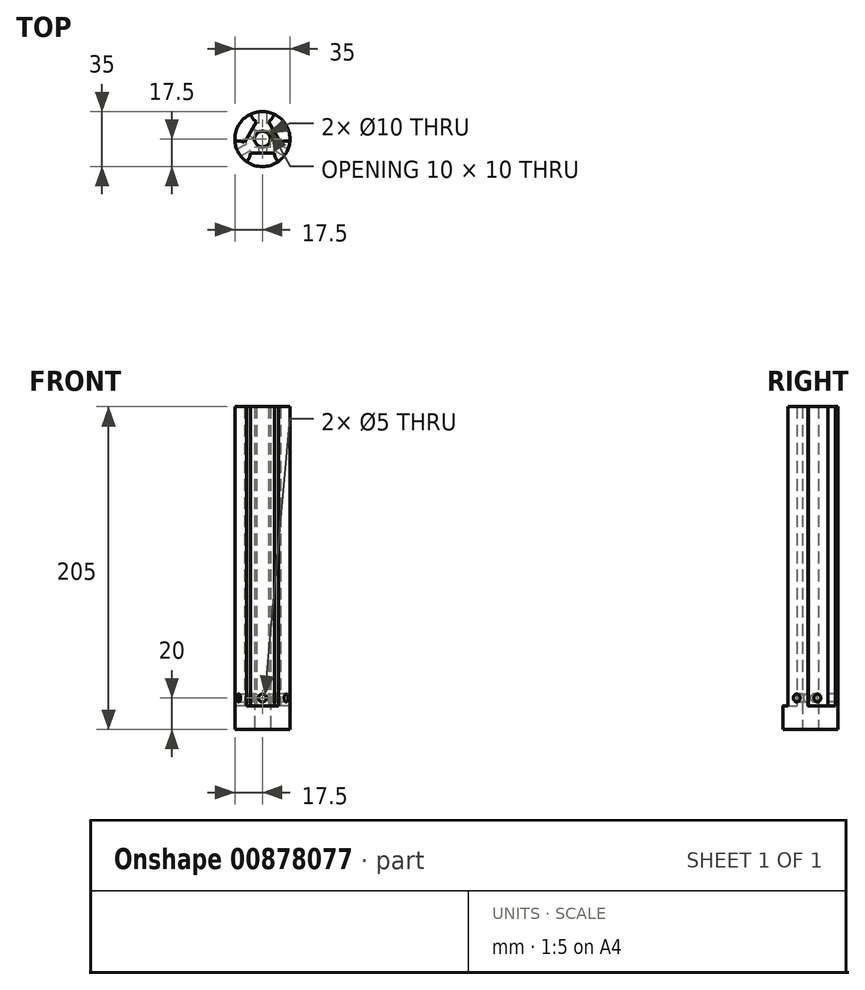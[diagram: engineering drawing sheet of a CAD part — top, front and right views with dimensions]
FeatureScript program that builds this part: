
annotation { "Feature Type Name" : "Feature", "Feature Type Description" : "" }
export const myFeature = defineFeature(function(context is Context, id is Id, definition is map)
    precondition{}
    {
        {
            var Q0;
            Q0=qCreatedBy(makeId("Top.planeOp"),FACE);
            var sketch = newSketch(context, id + "F0", { "sketchPlane" : qUnion([Q0])});
            skCircle(sketch, "E0", {"center": v(0, 0) * mm, "radius": 17.5 * mm});
            skCircle(sketch, "E1.cCircle", {"center": v(0, 0) * mm, "radius": 17.5 * mm, "construction": true});
            skLineSegment(sketch, "E1.0", {"start": v(0, 17.5) * mm, "end": v(15.16, -8.75) * mm});
            skLineSegment(sketch, "E1.1", {"start": v(15.16, -8.75) * mm, "end": v(-15.16, -8.75) * mm});
            skLineSegment(sketch, "E1.2", {"start": v(-15.16, -8.75) * mm, "end": v(0, 17.5) * mm});
            skCircle(sketch, "E2", {"center": v(-15.16, -8.75) * mm, "radius": 7.5 * mm});
            skCircle(sketch, "E3", {"center": v(0, 17.5) * mm, "radius": 7.5 * mm});
            skCircle(sketch, "E4", {"center": v(15.16, -8.75) * mm, "radius": 7.5 * mm});
            skPoint(sketch, "E5", {"position": v(-3.75, 11) * mm});
            skPoint(sketch, "E6", {"position": v(-11.4, -2.25) * mm});
            skCircle(sketch, "E7", {"center": v(0, 0) * mm, "radius": 5 * mm});
            skSolve(sketch);
        }
        {
            var Q0;
            {var subQ0=sQuery(id+"F0.wireOp",EDGE,"E3");var subQ1=sQuery(id+"F0.wireOp",EDGE,"E0");var subQ2=makeQuery(id+"F0.imprint","INTERSECT",VERTEX,{"disambiguationData":[OD(1.0)],"derivedFrom":[subQ1,subQ0]});Q0=makeQuery(id+"F0.imprint","IMPRINT",FACE,{"disambiguationData":[TD([[makeQuery(id+"F0.imprint","IMPRINT",EDGE,{"disambiguationData":[TD([[subQ2,-1.0]])],"derivedFrom":subQ1}),1.0]])]});}
            var Q1;
            {var subQ1=sQuery(id+"F0.wireOp",EDGE,"E0");var subQ3=sQuery(id+"F0.wireOp",EDGE,"E3");var subQ4=makeQuery(id+"F0.imprint","INTERSECT",VERTEX,{"disambiguationData":[OD(1.0)],"derivedFrom":[subQ1,subQ3]});Q1=makeQuery(id+"F0.imprint","IMPRINT",FACE,{"disambiguationData":[TD([[makeQuery(id+"F0.imprint","IMPRINT",EDGE,{"disambiguationData":[TD([[subQ4,-1.0]])],"derivedFrom":subQ3}),1.0]])]});}
            var Q2;
            {var subQ1=sQuery(id+"F0.wireOp",EDGE,"E1.0");var subQ3=sQuery(id+"F0.wireOp",EDGE,"E3");var subQ4=makeQuery(id+"F0.imprint","INTERSECT",VERTEX,{"derivedFrom":[subQ1,subQ3]});Q2=makeQuery(id+"F0.imprint","IMPRINT",FACE,{"disambiguationData":[TD([[makeQuery(id+"F0.imprint","IMPRINT",EDGE,{"disambiguationData":[TD([[subQ4,1.0]])],"derivedFrom":subQ3}),1.0]])]});}
            var Q3;
            {var subQ1=sQuery(id+"F0.wireOp",EDGE,"E0");var subQ3=sQuery(id+"F0.wireOp",EDGE,"E3");var subQ4=makeQuery(id+"F0.imprint","INTERSECT",VERTEX,{"disambiguationData":[OD(0.0)],"derivedFrom":[subQ1,subQ3]});Q3=makeQuery(id+"F0.imprint","IMPRINT",FACE,{"disambiguationData":[TD([[makeQuery(id+"F0.imprint","IMPRINT",EDGE,{"disambiguationData":[TD([[subQ4,1.0]])],"derivedFrom":subQ3}),1.0]])]});}
            var Q4;
            {var subQ0=sQuery(id+"F0.wireOp",EDGE,"E3");var subQ1=sQuery(id+"F0.wireOp",EDGE,"E0");var subQ2=makeQuery(id+"F0.imprint","INTERSECT",VERTEX,{"disambiguationData":[OD(0.0)],"derivedFrom":[subQ1,subQ0]});Q4=makeQuery(id+"F0.imprint","IMPRINT",FACE,{"disambiguationData":[TD([[makeQuery(id+"F0.imprint","IMPRINT",EDGE,{"disambiguationData":[TD([[subQ2,1.0]])],"derivedFrom":subQ1}),1.0]])]});}
            var Q5;
            Q5=makeQuery(id+"F0.imprint","IMPRINT",FACE,{"disambiguationData":[TD([[makeQuery(id+"F0.imprint","IMPRINT",EDGE,{"derivedFrom":sQuery(id+"F0.wireOp",EDGE,"E7")}),-1.0]])]});
            var Q6;
            {var subQ1=sQuery(id+"F0.wireOp",EDGE,"E1.1");var subQ3=sQuery(id+"F0.wireOp",EDGE,"E2");var subQ4=makeQuery(id+"F0.imprint","INTERSECT",VERTEX,{"derivedFrom":[subQ1,subQ3]});Q6=makeQuery(id+"F0.imprint","IMPRINT",FACE,{"disambiguationData":[TD([[makeQuery(id+"F0.imprint","IMPRINT",EDGE,{"disambiguationData":[TD([[subQ4,-1.0]])],"derivedFrom":subQ3}),1.0]])]});}
            var Q7;
            {var subQ1=sQuery(id+"F0.wireOp",EDGE,"E0");var subQ3=sQuery(id+"F0.wireOp",EDGE,"E2");var subQ4=makeQuery(id+"F0.imprint","INTERSECT",VERTEX,{"disambiguationData":[OD(0.0)],"derivedFrom":[subQ1,subQ3]});Q7=makeQuery(id+"F0.imprint","IMPRINT",FACE,{"disambiguationData":[TD([[makeQuery(id+"F0.imprint","IMPRINT",EDGE,{"disambiguationData":[TD([[subQ4,1.0]])],"derivedFrom":subQ3}),1.0]])]});}
            var Q8;
            {var subQ0=sQuery(id+"F0.wireOp",EDGE,"E2");var subQ1=sQuery(id+"F0.wireOp",EDGE,"E0");var subQ2=makeQuery(id+"F0.imprint","INTERSECT",VERTEX,{"disambiguationData":[OD(1.0)],"derivedFrom":[subQ1,subQ0]});Q8=makeQuery(id+"F0.imprint","IMPRINT",FACE,{"disambiguationData":[TD([[makeQuery(id+"F0.imprint","IMPRINT",EDGE,{"disambiguationData":[TD([[subQ2,-1.0]])],"derivedFrom":subQ1}),1.0]])]});}
            var Q9;
            {var subQ1=sQuery(id+"F0.wireOp",EDGE,"E0");var subQ3=sQuery(id+"F0.wireOp",EDGE,"E2");var subQ4=makeQuery(id+"F0.imprint","INTERSECT",VERTEX,{"disambiguationData":[OD(1.0)],"derivedFrom":[subQ1,subQ3]});Q9=makeQuery(id+"F0.imprint","IMPRINT",FACE,{"disambiguationData":[TD([[makeQuery(id+"F0.imprint","IMPRINT",EDGE,{"disambiguationData":[TD([[subQ4,-1.0]])],"derivedFrom":subQ3}),1.0]])]});}
            var Q10;
            {var subQ1=sQuery(id+"F0.wireOp",EDGE,"E0");var subQ3=sQuery(id+"F0.wireOp",EDGE,"E4");var subQ4=makeQuery(id+"F0.imprint","INTERSECT",VERTEX,{"disambiguationData":[OD(0.0)],"derivedFrom":[subQ1,subQ3]});Q10=makeQuery(id+"F0.imprint","IMPRINT",FACE,{"disambiguationData":[TD([[makeQuery(id+"F0.imprint","IMPRINT",EDGE,{"disambiguationData":[TD([[subQ4,1.0]])],"derivedFrom":subQ3}),1.0]])]});}
            var Q11;
            {var subQ1=sQuery(id+"F0.wireOp",EDGE,"E1.0");var subQ3=sQuery(id+"F0.wireOp",EDGE,"E4");var subQ4=makeQuery(id+"F0.imprint","INTERSECT",VERTEX,{"derivedFrom":[subQ1,subQ3]});Q11=makeQuery(id+"F0.imprint","IMPRINT",FACE,{"disambiguationData":[TD([[makeQuery(id+"F0.imprint","IMPRINT",EDGE,{"disambiguationData":[TD([[subQ4,-1.0]])],"derivedFrom":subQ3}),1.0]])]});}
            var Q12;
            {var subQ1=sQuery(id+"F0.wireOp",EDGE,"E0");var subQ3=sQuery(id+"F0.wireOp",EDGE,"E4");var subQ4=makeQuery(id+"F0.imprint","INTERSECT",VERTEX,{"disambiguationData":[OD(1.0)],"derivedFrom":[subQ1,subQ3]});Q12=makeQuery(id+"F0.imprint","IMPRINT",FACE,{"disambiguationData":[TD([[makeQuery(id+"F0.imprint","IMPRINT",EDGE,{"disambiguationData":[TD([[subQ4,-1.0]])],"derivedFrom":subQ3}),1.0]])]});}
            extrude(context, id + "F1", {"entities" : qUnion([Q0, Q1, Q2, Q3, Q4, Q5, Q6, Q7, Q8, Q9, Q10, Q11, Q12]), "depth" : 15 * mm, "offsetDistance" : 25 * mm});
        }
        {
            var Q0;
            {var subQ1=sQuery(id+"F0.wireOp",EDGE,"E0");var subQ3=sQuery(id+"F0.wireOp",EDGE,"E3");var subQ4=makeQuery(id+"F0.imprint","INTERSECT",VERTEX,{"disambiguationData":[OD(1.0)],"derivedFrom":[subQ1,subQ3]});Q0=makeQuery(id+"F0.imprint","IMPRINT",FACE,{"disambiguationData":[TD([[makeQuery(id+"F0.imprint","IMPRINT",EDGE,{"disambiguationData":[TD([[subQ4,-1.0]])],"derivedFrom":subQ3}),1.0]])]});}
            var Q1;
            {var subQ1=sQuery(id+"F0.wireOp",EDGE,"E1.0");var subQ3=sQuery(id+"F0.wireOp",EDGE,"E3");var subQ4=makeQuery(id+"F0.imprint","INTERSECT",VERTEX,{"derivedFrom":[subQ1,subQ3]});Q1=makeQuery(id+"F0.imprint","IMPRINT",FACE,{"disambiguationData":[TD([[makeQuery(id+"F0.imprint","IMPRINT",EDGE,{"disambiguationData":[TD([[subQ4,1.0]])],"derivedFrom":subQ3}),1.0]])]});}
            var Q2;
            {var subQ1=sQuery(id+"F0.wireOp",EDGE,"E0");var subQ3=sQuery(id+"F0.wireOp",EDGE,"E3");var subQ4=makeQuery(id+"F0.imprint","INTERSECT",VERTEX,{"disambiguationData":[OD(0.0)],"derivedFrom":[subQ1,subQ3]});Q2=makeQuery(id+"F0.imprint","IMPRINT",FACE,{"disambiguationData":[TD([[makeQuery(id+"F0.imprint","IMPRINT",EDGE,{"disambiguationData":[TD([[subQ4,1.0]])],"derivedFrom":subQ3}),1.0]])]});}
            var Q3;
            Q3=makeQuery(id+"F0.imprint","IMPRINT",FACE,{"disambiguationData":[TD([[makeQuery(id+"F0.imprint","IMPRINT",EDGE,{"derivedFrom":sQuery(id+"F0.wireOp",EDGE,"E7")}),-1.0]])]});
            var Q4;
            {var subQ1=sQuery(id+"F0.wireOp",EDGE,"E1.0");var subQ3=sQuery(id+"F0.wireOp",EDGE,"E4");var subQ4=makeQuery(id+"F0.imprint","INTERSECT",VERTEX,{"derivedFrom":[subQ1,subQ3]});Q4=makeQuery(id+"F0.imprint","IMPRINT",FACE,{"disambiguationData":[TD([[makeQuery(id+"F0.imprint","IMPRINT",EDGE,{"disambiguationData":[TD([[subQ4,-1.0]])],"derivedFrom":subQ3}),1.0]])]});}
            var Q5;
            {var subQ1=sQuery(id+"F0.wireOp",EDGE,"E1.1");var subQ3=sQuery(id+"F0.wireOp",EDGE,"E2");var subQ4=makeQuery(id+"F0.imprint","INTERSECT",VERTEX,{"derivedFrom":[subQ1,subQ3]});Q5=makeQuery(id+"F0.imprint","IMPRINT",FACE,{"disambiguationData":[TD([[makeQuery(id+"F0.imprint","IMPRINT",EDGE,{"disambiguationData":[TD([[subQ4,-1.0]])],"derivedFrom":subQ3}),1.0]])]});}
            var Q6;
            {var subQ1=sQuery(id+"F0.wireOp",EDGE,"E0");var subQ3=sQuery(id+"F0.wireOp",EDGE,"E2");var subQ4=makeQuery(id+"F0.imprint","INTERSECT",VERTEX,{"disambiguationData":[OD(0.0)],"derivedFrom":[subQ1,subQ3]});Q6=makeQuery(id+"F0.imprint","IMPRINT",FACE,{"disambiguationData":[TD([[makeQuery(id+"F0.imprint","IMPRINT",EDGE,{"disambiguationData":[TD([[subQ4,1.0]])],"derivedFrom":subQ3}),1.0]])]});}
            var Q7;
            {var subQ1=sQuery(id+"F0.wireOp",EDGE,"E0");var subQ3=sQuery(id+"F0.wireOp",EDGE,"E2");var subQ4=makeQuery(id+"F0.imprint","INTERSECT",VERTEX,{"disambiguationData":[OD(1.0)],"derivedFrom":[subQ1,subQ3]});Q7=makeQuery(id+"F0.imprint","IMPRINT",FACE,{"disambiguationData":[TD([[makeQuery(id+"F0.imprint","IMPRINT",EDGE,{"disambiguationData":[TD([[subQ4,-1.0]])],"derivedFrom":subQ3}),1.0]])]});}
            var Q8;
            {var subQ1=sQuery(id+"F0.wireOp",EDGE,"E0");var subQ3=sQuery(id+"F0.wireOp",EDGE,"E4");var subQ4=makeQuery(id+"F0.imprint","INTERSECT",VERTEX,{"disambiguationData":[OD(0.0)],"derivedFrom":[subQ1,subQ3]});Q8=makeQuery(id+"F0.imprint","IMPRINT",FACE,{"disambiguationData":[TD([[makeQuery(id+"F0.imprint","IMPRINT",EDGE,{"disambiguationData":[TD([[subQ4,1.0]])],"derivedFrom":subQ3}),1.0]])]});}
            var Q9;
            {var subQ1=sQuery(id+"F0.wireOp",EDGE,"E0");var subQ3=sQuery(id+"F0.wireOp",EDGE,"E4");var subQ4=makeQuery(id+"F0.imprint","INTERSECT",VERTEX,{"disambiguationData":[OD(1.0)],"derivedFrom":[subQ1,subQ3]});Q9=makeQuery(id+"F0.imprint","IMPRINT",FACE,{"disambiguationData":[TD([[makeQuery(id+"F0.imprint","IMPRINT",EDGE,{"disambiguationData":[TD([[subQ4,-1.0]])],"derivedFrom":subQ3}),1.0]])]});}
            extrude(context, id + "F2", {"entities" : qUnion([Q0, Q1, Q2, Q3, Q4, Q5, Q6, Q7, Q8, Q9]), "operationType" : NewBodyOperationType.ADD, "depth" : 205 * mm, "offsetDistance" : 25 * mm});
        }
        {
            var Q0;
            Q0=makeQuery(id+"F2.opExtrude","SWEPT_FACE",FACE,{"disambiguationData":[OSD([sQuery(id+"F0.wireOp",EDGE,"E1.2")])]});
            var sketch = newSketch(context, id + "F3", { "sketchPlane" : qUnion([Q0])});
            skLineSegment(sketch, "E8.bottom", {"start": v(-7.66, 15) * mm, "end": v(7.66, 15) * mm});
            skLineSegment(sketch, "E8.top", {"start": v(-7.66, 20) * mm, "end": v(7.66, 20) * mm});
            skLineSegment(sketch, "E8.left", {"start": v(-7.66, 15) * mm, "end": v(-7.66, 20) * mm});
            skLineSegment(sketch, "E8.right", {"start": v(7.66, 15) * mm, "end": v(7.66, 20) * mm});
            skPoint(sketch, "E9", {"position": v(0, 20) * mm});
            skSolve(sketch);
        }
        {
            var Q0;
            Q0=sQuery(id+"F3.wireOp",VERTEX,"E9");
            var Q1;
            Q1=makeQuery(id+"F1.opExtrude","SWEPT_BODY",BODY,{"disambiguationData":[OSD([sQuery(id+"F0.wireOp",EDGE,"E0"),sQuery(id+"F0.wireOp",EDGE,"E7")])]});
            hole(context, id + "F4", {"style" : HoleStyle.SIMPLE, "endStyle" : HoleEndStyle.THROUGH, "holeDiameter" : 5 * mm, "majorDiameter" : 5 * mm, "isTappedThrough" : true, "tappedDepth" : 12 * mm, "tapClearance" : 3, "locations" : qUnion([Q0]), "scope" : qUnion([Q1])});
        }
        {
            var Q0;
            Q0=makeQuery(id+"F2.opExtrude","SWEPT_FACE",FACE,{"disambiguationData":[OSD([sQuery(id+"F0.wireOp",EDGE,"E1.0")])]});
            var sketch = newSketch(context, id + "F5", { "sketchPlane" : qUnion([Q0])});
            skLineSegment(sketch, "E10.bottom", {"start": v(-7.66, 15) * mm, "end": v(7.66, 15) * mm});
            skLineSegment(sketch, "E10.top", {"start": v(-7.66, 20) * mm, "end": v(7.66, 20) * mm});
            skLineSegment(sketch, "E10.left", {"start": v(-7.66, 15) * mm, "end": v(-7.66, 20) * mm});
            skLineSegment(sketch, "E10.right", {"start": v(7.66, 15) * mm, "end": v(7.66, 20) * mm});
            skPoint(sketch, "E11", {"position": v(0, 20) * mm});
            skSolve(sketch);
        }
        {
            var Q0;
            Q0=makeQuery(id+"F2.opExtrude","SWEPT_FACE",FACE,{"disambiguationData":[OSD([sQuery(id+"F0.wireOp",EDGE,"E1.1")])]});
            var sketch = newSketch(context, id + "F6", { "sketchPlane" : qUnion([Q0])});
            skLineSegment(sketch, "E12.bottom", {"start": v(-7.66, 15) * mm, "end": v(7.66, 15) * mm});
            skLineSegment(sketch, "E12.top", {"start": v(-7.66, 20) * mm, "end": v(7.66, 20) * mm});
            skLineSegment(sketch, "E12.left", {"start": v(-7.66, 15) * mm, "end": v(-7.66, 20) * mm});
            skLineSegment(sketch, "E12.right", {"start": v(7.66, 15) * mm, "end": v(7.66, 20) * mm});
            skPoint(sketch, "E13", {"position": v(0, 20) * mm});
            skSolve(sketch);
        }
        {
            var Q0;
            Q0=sQuery(id+"F6.wireOp",VERTEX,"E13");
            var Q1;
            Q1=makeQuery(id+"F1.opExtrude","SWEPT_BODY",BODY,{"disambiguationData":[OSD([sQuery(id+"F0.wireOp",EDGE,"E0"),sQuery(id+"F0.wireOp",EDGE,"E7")])]});
            hole(context, id + "F7", {"style" : HoleStyle.SIMPLE, "endStyle" : HoleEndStyle.THROUGH, "holeDiameter" : 5 * mm, "majorDiameter" : 5 * mm, "isTappedThrough" : true, "tappedDepth" : 12 * mm, "tapClearance" : 3, "locations" : qUnion([Q0]), "scope" : qUnion([Q1])});
        }
        {
            var Q0;
            Q0=sQuery(id+"F5.wireOp",VERTEX,"E11");
            var Q1;
            Q1=makeQuery(id+"F1.opExtrude","SWEPT_BODY",BODY,{"disambiguationData":[OSD([sQuery(id+"F0.wireOp",EDGE,"E0"),sQuery(id+"F0.wireOp",EDGE,"E7")])]});
            hole(context, id + "F8", {"style" : HoleStyle.SIMPLE, "endStyle" : HoleEndStyle.THROUGH, "holeDiameter" : 5 * mm, "majorDiameter" : 5 * mm, "isTappedThrough" : true, "tappedDepth" : 12 * mm, "tapClearance" : 3, "locations" : qUnion([Q0]), "scope" : qUnion([Q1])});
        }
    });
